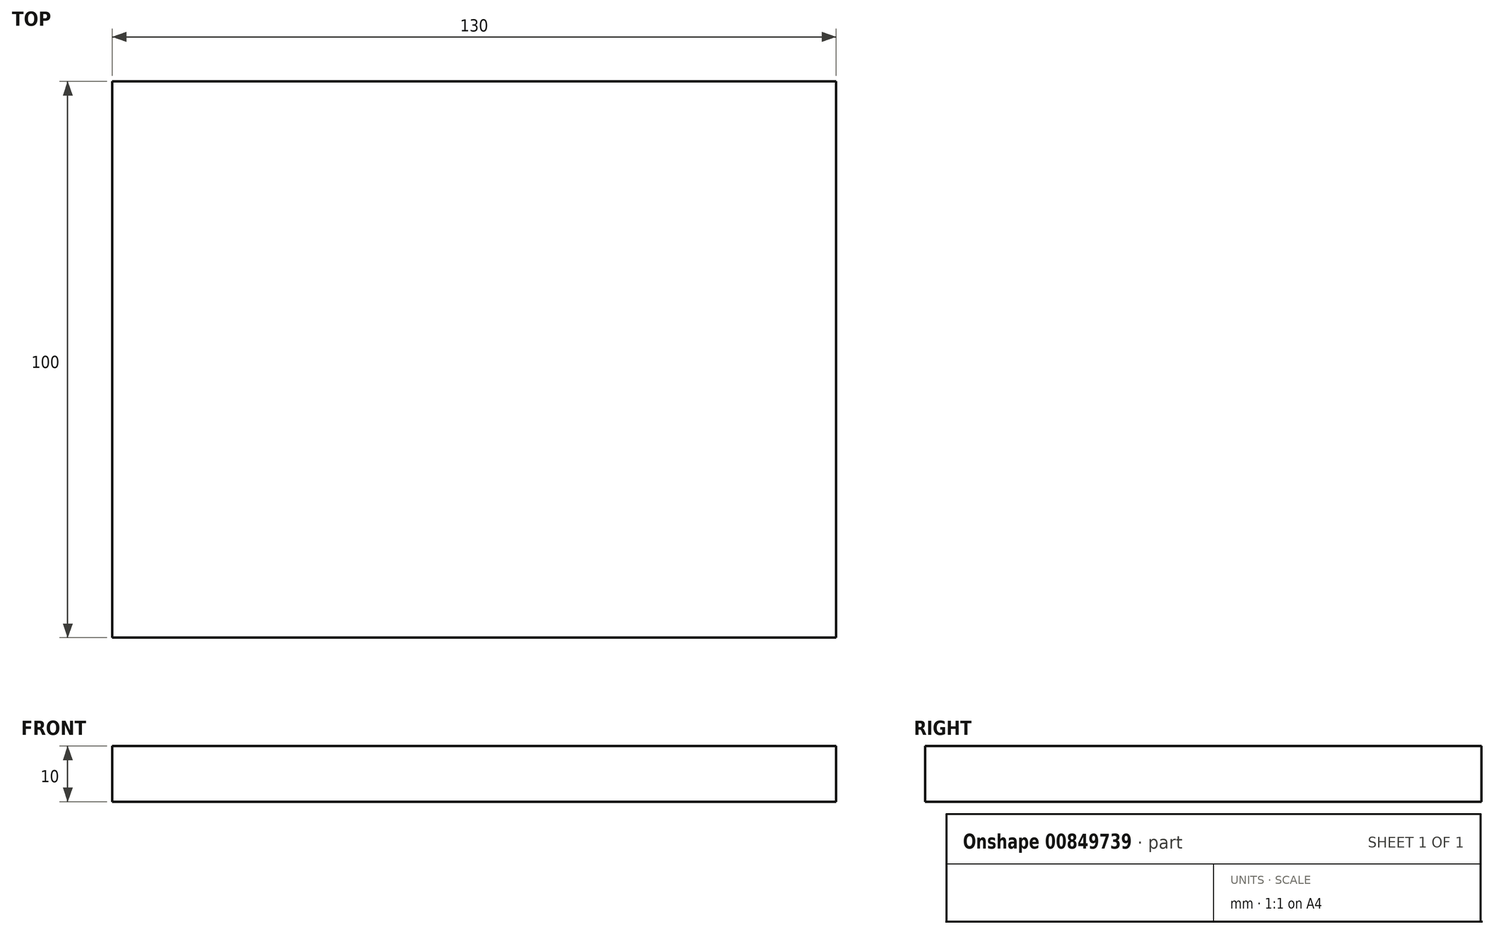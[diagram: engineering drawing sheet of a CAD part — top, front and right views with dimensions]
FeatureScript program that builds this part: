
annotation { "Feature Type Name" : "Feature", "Feature Type Description" : "" }
export const myFeature = defineFeature(function(context is Context, id is Id, definition is map)
    precondition{}
    {
        {
            var Q0;
            Q0=qCreatedBy(makeId("Top.planeOp"),FACE);
            var sketch = newSketch(context, id + "F0", { "sketchPlane" : qUnion([Q0])});
            skLineSegment(sketch, "E0.bottom", {"start": v(65, -50) * mm, "end": v(-65, -50) * mm});
            skLineSegment(sketch, "E0.top", {"start": v(65, 50) * mm, "end": v(-65, 50) * mm});
            skLineSegment(sketch, "E0.left", {"start": v(65, -50) * mm, "end": v(65, 50) * mm});
            skLineSegment(sketch, "E0.right", {"start": v(-65, -50) * mm, "end": v(-65, 50) * mm});
            skPoint(sketch, "E0.middle", {"position": v(0, 0) * mm});
            skSolve(sketch);
        }
        {
            var Q0;
            Q0 = qSketchRegion(id + "F0", true);
            extrude(context, id + "F1", {"entities" : qUnion([Q0]), "oppositeDirection" : true, "depth" : 10 * mm, "offsetDistance" : 25 * mm});
        }
    });
